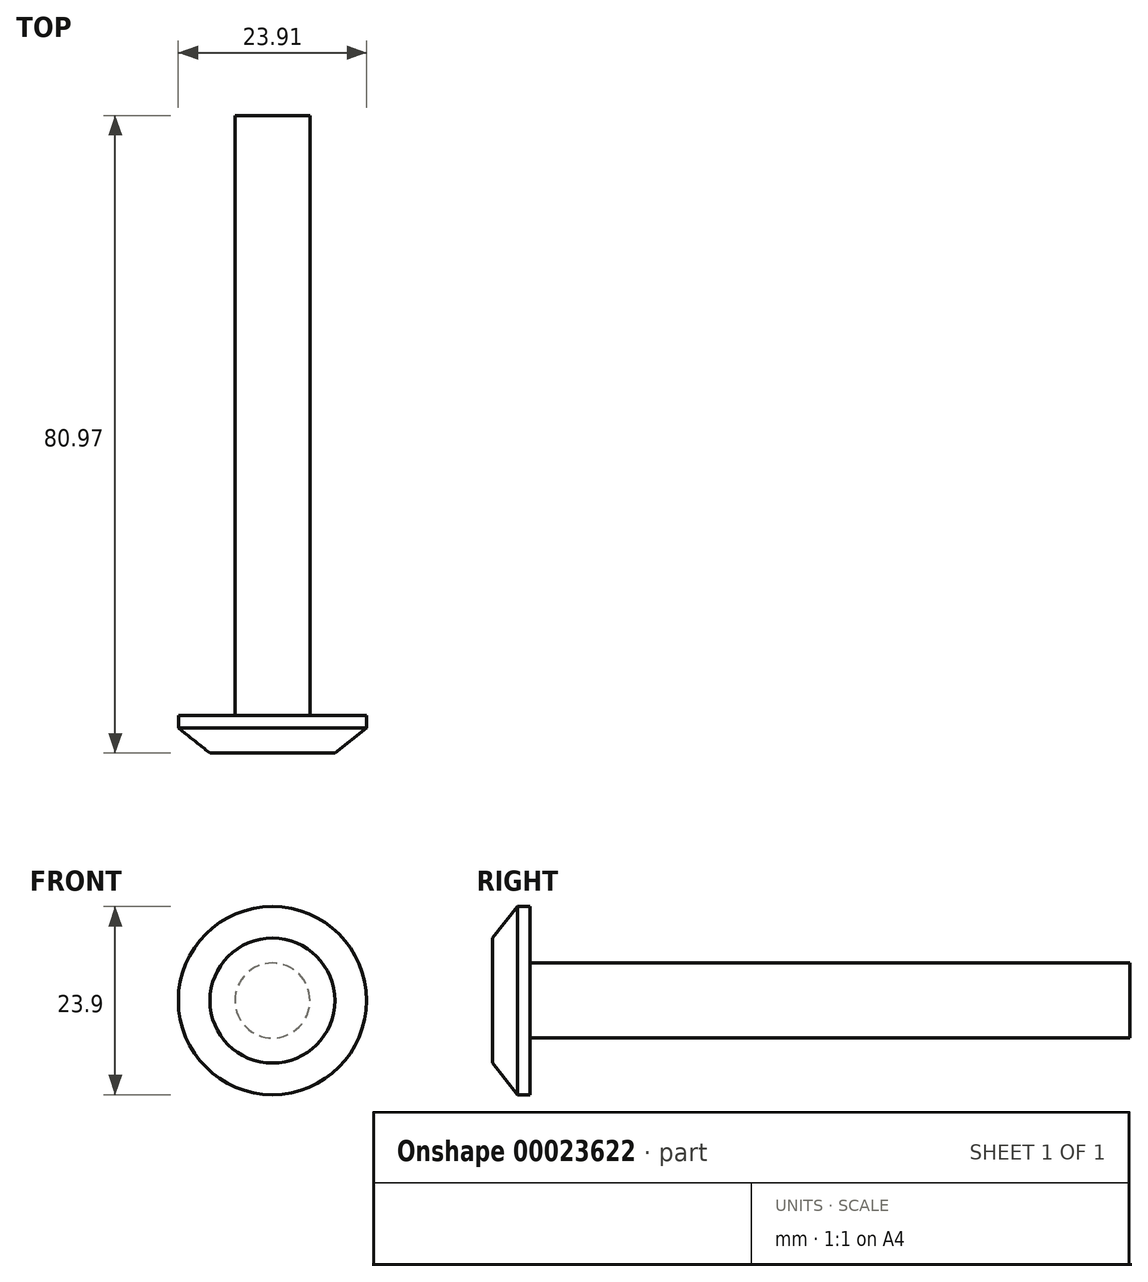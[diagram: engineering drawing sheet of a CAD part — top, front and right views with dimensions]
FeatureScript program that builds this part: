
annotation { "Feature Type Name" : "Feature", "Feature Type Description" : "" }
export const myFeature = defineFeature(function(context is Context, id is Id, definition is map)
    precondition{}
    {
        {
            var Q0;
            Q0=qCreatedBy(makeId("Top.planeOp"),FACE);
            var sketch = newSketch(context, id + "F0", { "sketchPlane" : qUnion([Q0])});
            skLineSegment(sketch, "E0", {"start": v(-6.21, 60.37) * mm, "end": v(-6.21, -15.83) * mm});
            skLineSegment(sketch, "E1", {"start": v(-6.21, 60.37) * mm, "end": v(-10.97, 60.37) * mm});
            skLineSegment(sketch, "E2", {"start": v(-10.97, 60.37) * mm, "end": v(-10.97, -15.83) * mm});
            skLineSegment(sketch, "E3", {"start": v(-6.21, -15.83) * mm, "end": v(-6.21, -20.6) * mm});
            skLineSegment(sketch, "E4", {"start": v(-10.97, -15.83) * mm, "end": v(-18.17, -15.83) * mm});
            skLineSegment(sketch, "E5", {"start": v(-18.17, -15.83) * mm, "end": v(-18.17, -17.42) * mm});
            skLineSegment(sketch, "E6", {"start": v(-6.21, -20.6) * mm, "end": v(-14.15, -20.6) * mm});
            skLineSegment(sketch, "E7", {"start": v(-18.17, -17.42) * mm, "end": v(-14.15, -20.6) * mm});
            skSolve(sketch);
        }
        {
            var Q0;
            Q0=makeQuery(id+"F0.imprint","IMPRINT",FACE,{"disambiguationData":[TD([[makeQuery(id+"F0.imprint","IMPRINT",EDGE,{"derivedFrom":sQuery(id+"F0.wireOp",EDGE,"E0")}),-1.0]])]});
            var Q1;
            Q1=sQuery(id+"F0.wireOp",EDGE,"E0");
            revolve(context, id + "F1", {"entities" : qUnion([Q0]), "axis" : qUnion([Q1]), "revolveType" : RevolveType.FULL});
        }
    });
